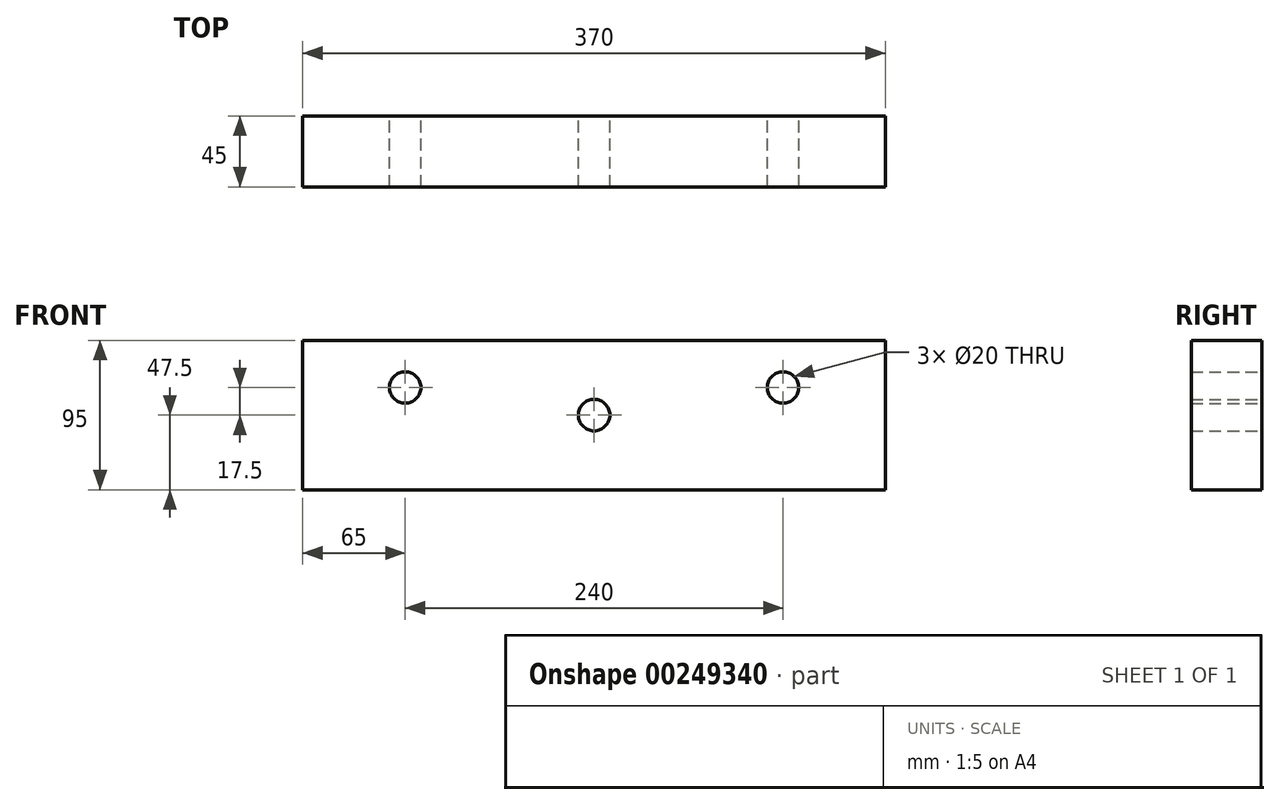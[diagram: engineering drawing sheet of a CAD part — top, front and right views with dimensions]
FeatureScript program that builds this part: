
annotation { "Feature Type Name" : "Feature", "Feature Type Description" : "" }
export const myFeature = defineFeature(function(context is Context, id is Id, definition is map)
    precondition{}
    {
        {
            var Q0;
            Q0=qCreatedBy(makeId("Front.planeOp"),FACE);
            var sketch = newSketch(context, id + "F0", { "sketchPlane" : qUnion([Q0])});
            skLineSegment(sketch, "E0.bottom", {"start": v(-185, 47.5) * mm, "end": v(185, 47.5) * mm});
            skLineSegment(sketch, "E0.top", {"start": v(-185, -47.5) * mm, "end": v(185, -47.5) * mm});
            skLineSegment(sketch, "E0.left", {"start": v(-185, 47.5) * mm, "end": v(-185, -47.5) * mm});
            skLineSegment(sketch, "E0.right", {"start": v(185, 47.5) * mm, "end": v(185, -47.5) * mm});
            skPoint(sketch, "E0.middle", {"position": v(0, 0) * mm});
            skCircle(sketch, "E1", {"center": v(-120, 17.5) * mm, "radius": 10 * mm});
            skCircle(sketch, "E2", {"center": v(120, 17.5) * mm, "radius": 10 * mm});
            skCircle(sketch, "E3", {"center": v(0, 0) * mm, "radius": 10 * mm});
            skSolve(sketch);
        }
        {
            var Q0;
            Q0=makeQuery(id+"F0.imprint","IMPRINT",FACE,{"disambiguationData":[TD([[makeQuery(id+"F0.imprint","IMPRINT",EDGE,{"derivedFrom":sQuery(id+"F0.wireOp",EDGE,"E0.bottom")}),-1.0]])]});
            extrude(context, id + "F1", {"entities" : qUnion([Q0]), "depth" : 45 * mm});
        }
    });
